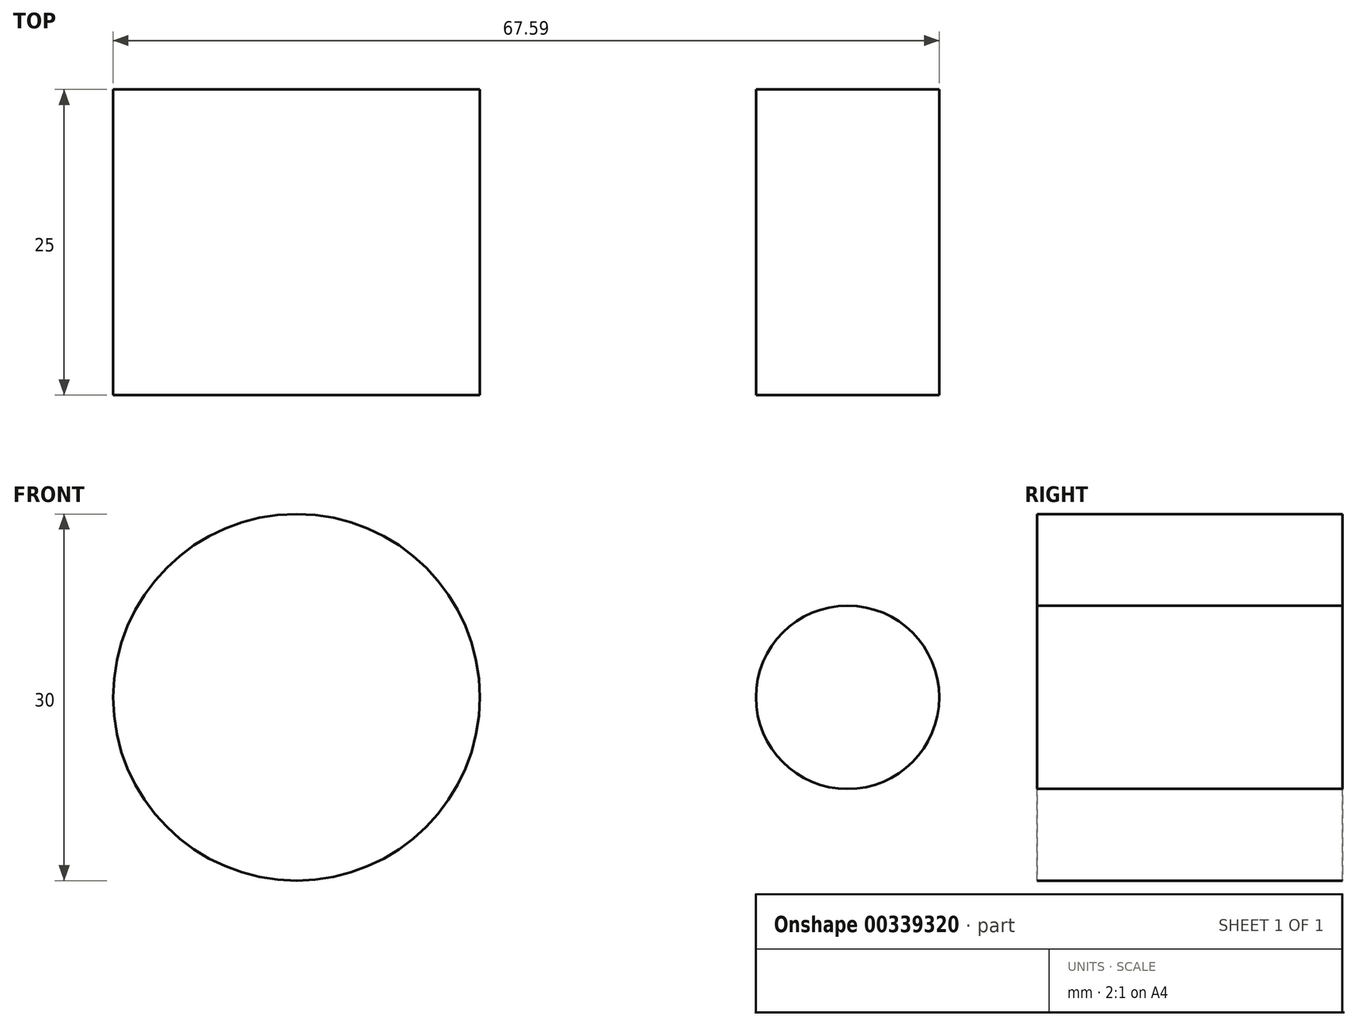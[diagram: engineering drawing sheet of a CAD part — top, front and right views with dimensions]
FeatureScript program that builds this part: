
annotation { "Feature Type Name" : "Feature", "Feature Type Description" : "" }
export const myFeature = defineFeature(function(context is Context, id is Id, definition is map)
    precondition{}
    {
        {
            var Q0;
            Q0=qCreatedBy(makeId("Front.planeOp"),FACE);
            var sketch = newSketch(context, id + "F0", { "sketchPlane" : qUnion([Q0])});
            skCircle(sketch, "E0", {"center": v(37.32, 25.71) * mm, "radius": 15 * mm});
            skCircle(sketch, "E1", {"center": v(82.41, 25.71) * mm, "radius": 7.5 * mm});
            skArc(sketch, "E2", {"start": v(37.32, 41.71) * mm, "mid": v(21.32, 25.71) * mm, "end": v(37.32, 9.71) * mm});
            skArc(sketch, "E3", {"start": v(82.41, 34.21) * mm, "mid": v(90.91, 25.71) * mm, "end": v(82.41, 17.21) * mm});
            skLineSegment(sketch, "E4", {"start": v(82.41, 34.21) * mm, "end": v(37.32, 41.71) * mm});
            skLineSegment(sketch, "E5", {"start": v(82.41, 17.21) * mm, "end": v(37.32, 9.71) * mm});
            skSolve(sketch);
        }
        {
            var Q0;
            Q0=makeQuery(id+"F0.imprint","IMPRINT",FACE,{"disambiguationData":[TD([[makeQuery(id+"F0.imprint","IMPRINT",EDGE,{"derivedFrom":sQuery(id+"F0.wireOp",EDGE,"E0")}),1.0]])]});
            var Q1;
            Q1=makeQuery(id+"F0.imprint","IMPRINT",FACE,{"disambiguationData":[TD([[makeQuery(id+"F0.imprint","IMPRINT",EDGE,{"derivedFrom":sQuery(id+"F0.wireOp",EDGE,"E1")}),1.0]])]});
            extrude(context, id + "F1", {"entities" : qUnion([Q0, Q1]), "endBound" : BoundingType.SYMMETRIC, "depth" : 25 * mm});
        }
        {
            var Q0;
            Q0=sQuery(id+"F0.wireOp",EDGE,"E2");
            var Q1;
            Q1=sQuery(id+"F0.wireOp",EDGE,"E4");
            var Q2;
            Q2=sQuery(id+"F0.wireOp",EDGE,"E5");
            var Q3;
            Q3=sQuery(id+"F0.wireOp",EDGE,"E3");
            extrude(context, id + "F2", {"bodyType" : ToolBodyType.SURFACE, "surfaceEntities" : qUnion([Q0, Q1, Q2, Q3]), "endBound" : BoundingType.SYMMETRIC, "depth" : 25 * mm});
        }
    });
